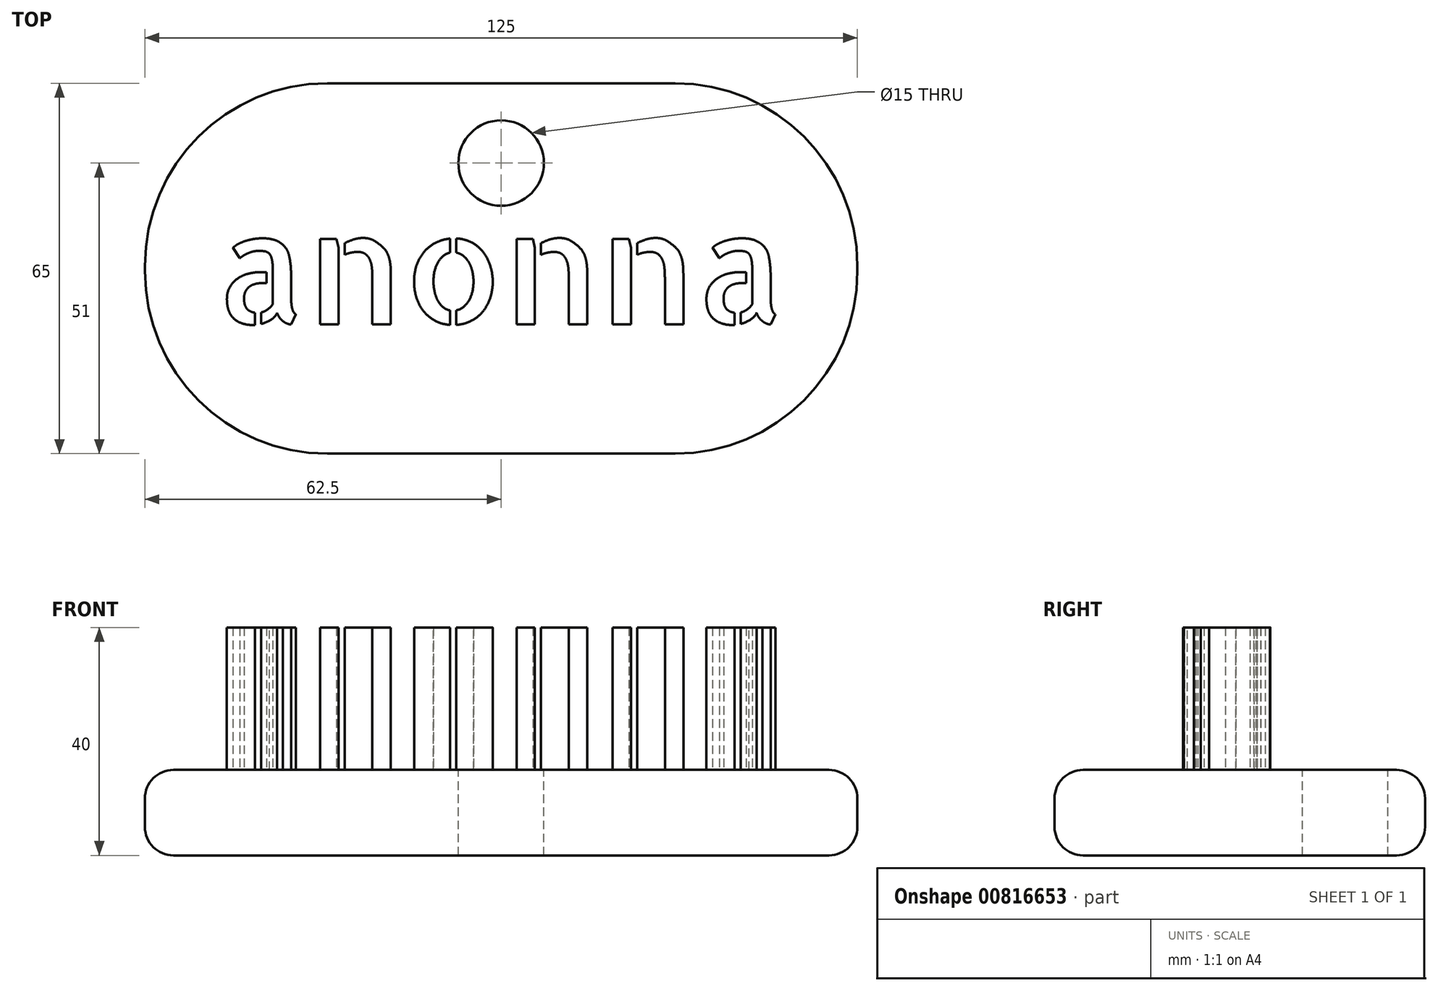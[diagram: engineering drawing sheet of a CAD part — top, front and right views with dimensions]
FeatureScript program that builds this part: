
annotation { "Feature Type Name" : "Feature", "Feature Type Description" : "" }
export const myFeature = defineFeature(function(context is Context, id is Id, definition is map)
    precondition{}
    {
        {
            var Q0;
            Q0=qCreatedBy(makeId("Top.planeOp"),FACE);
            var sketch = newSketch(context, id + "F0", { "sketchPlane" : qUnion([Q0])});
            skLineSegment(sketch, "E0.bottom", {"start": v(62.5, 32.5) * mm, "end": v(-62.5, 32.5) * mm});
            skLineSegment(sketch, "E0.top", {"start": v(62.5, -32.5) * mm, "end": v(-62.5, -32.5) * mm});
            skLineSegment(sketch, "E0.left", {"start": v(62.5, 32.5) * mm, "end": v(62.5, -32.5) * mm});
            skLineSegment(sketch, "E0.right", {"start": v(-62.5, 32.5) * mm, "end": v(-62.5, -32.5) * mm});
            skPoint(sketch, "E0.middle", {"position": v(0, 0) * mm});
            skSolve(sketch);
        }
        {
            var Q0;
            Q0=makeQuery(id+"F0.imprint","IMPRINT",FACE,{"disambiguationData":[TD([[makeQuery(id+"F0.imprint","IMPRINT",EDGE,{"derivedFrom":sQuery(id+"F0.wireOp",EDGE,"E0.bottom")}),1.0]])]});
            extrude(context, id + "F1", {"entities" : qUnion([Q0]), "depth" : 15 * mm, "offsetDistance" : 25 * mm});
        }
        {
            var Q0;
            Q0=makeQuery(id+"F1.opExtrude","CAP_FACE",FACE,{"disambiguationData":[OSD([sQuery(id+"F0.wireOp",EDGE,"E0.bottom"),sQuery(id+"F0.wireOp",EDGE,"E0.top"),sQuery(id+"F0.wireOp",EDGE,"E0.left"),sQuery(id+"F0.wireOp",EDGE,"E0.right")])],"isStart":false});
            var sketch = newSketch(context, id + "F2", { "sketchPlane" : qUnion([Q0])});
            skText(sketch, "E1", { "text": "anonna", "fontName": "AllertaStencil-Regular.ttf"});
            skLineSegment(sketch, "E2", {"start": v(-50, 0) * mm, "end": v(-62.5, 0) * mm, "construction": true});
            skLineSegment(sketch, "E3", {"start": v(0, -9.8) * mm, "end": v(0, -32.5) * mm, "construction": true});
            skLineSegment(sketch, "E4", {"start": v(0, 9.8) * mm, "end": v(0, 32.5) * mm, "construction": true});
            skLineSegment(sketch, "E5", {"start": v(50, 0) * mm, "end": v(62.5, 0) * mm, "construction": true});
            const initialGuessF2  = {"E1": [-0.05, -0.0098, 1, 0, 0.0196]};
            skSetInitialGuess(sketch, initialGuessF2);
            skSolve(sketch);
        }
        {
            var Q0;
            Q0 = qSketchRegion(id + "F2", true);
            extrude(context, id + "F3", {"entities" : qUnion([Q0]), "operationType" : NewBodyOperationType.ADD, "depth" : 25 * mm, "offsetDistance" : 25 * mm});
        }
        {
            var Q0;
            Q0=makeQuery(id+"F1.opExtrude","CAP_FACE",FACE,{"disambiguationData":[OSD([sQuery(id+"F0.wireOp",EDGE,"E0.bottom"),sQuery(id+"F0.wireOp",EDGE,"E0.top"),sQuery(id+"F0.wireOp",EDGE,"E0.left"),sQuery(id+"F0.wireOp",EDGE,"E0.right")])],"isStart":false});
            var sketch = newSketch(context, id + "F4", { "sketchPlane" : qUnion([Q0])});
            skCircle(sketch, "E6", {"center": v(0, 18.5) * mm, "radius": 7.5 * mm});
            skLineSegment(sketch, "E7", {"start": v(0, 32.5) * mm, "end": v(0, 18.5) * mm, "construction": true});
            skLineSegment(sketch, "E8", {"start": v(0, 32.5) * mm, "end": v(0, 18.5) * mm});
            skSolve(sketch);
        }
        {
            var Q0;
            Q0 = qSketchRegion(id + "F4", true);
            extrude(context, id + "F5", {"entities" : qUnion([Q0]), "operationType" : NewBodyOperationType.REMOVE, "oppositeDirection" : true, "depth" : 30 * mm, "offsetDistance" : 25 * mm});
        }
        {
            var Q0;
            Q0=makeQuery(id+"F1.opExtrude","SWEPT_EDGE",EDGE,{"disambiguationData":[OSD([sQuery(id+"F0.wireOp",EDGE,"E0.bottom"),sQuery(id+"F0.wireOp",EDGE,"E0.right")])]});
            var Q1;
            Q1=makeQuery(id+"F1.opExtrude","SWEPT_EDGE",EDGE,{"disambiguationData":[OSD([sQuery(id+"F0.wireOp",EDGE,"E0.top"),sQuery(id+"F0.wireOp",EDGE,"E0.right")])]});
            var Q2;
            Q2=makeQuery(id+"F1.opExtrude","SWEPT_EDGE",EDGE,{"disambiguationData":[OSD([sQuery(id+"F0.wireOp",EDGE,"E0.bottom"),sQuery(id+"F0.wireOp",EDGE,"E0.left")])]});
            var Q3;
            Q3=makeQuery(id+"F1.opExtrude","SWEPT_EDGE",EDGE,{"disambiguationData":[OSD([sQuery(id+"F0.wireOp",EDGE,"E0.top"),sQuery(id+"F0.wireOp",EDGE,"E0.left")])]});
            fillet(context, id + "F6", {"entities" : qUnion([Q0, Q1, Q2, Q3]), "radius" : 32 * mm, "tangentPropagation" : true, "allowEdgeOverflow" : false});
        }
        {
            var Q0;
            Q0=makeQuery(id+"F1.opExtrude","CAP_EDGE",EDGE,{"disambiguationData":[OSD([sQuery(id+"F0.wireOp",EDGE,"E0.top")])],"isStart":false});
            fillet(context, id + "F7", {"entities" : qUnion([Q0]), "radius" : 5 * mm, "tangentPropagation" : true, "allowEdgeOverflow" : false});
        }
        {
            var Q0;
            Q0=makeQuery(id+"F1.opExtrude","CAP_EDGE",EDGE,{"disambiguationData":[OSD([sQuery(id+"F0.wireOp",EDGE,"E0.top")])],"isStart":true});
            fillet(context, id + "F8", {"entities" : qUnion([Q0]), "radius" : 5 * mm, "tangentPropagation" : true, "allowEdgeOverflow" : false});
        }
    });
